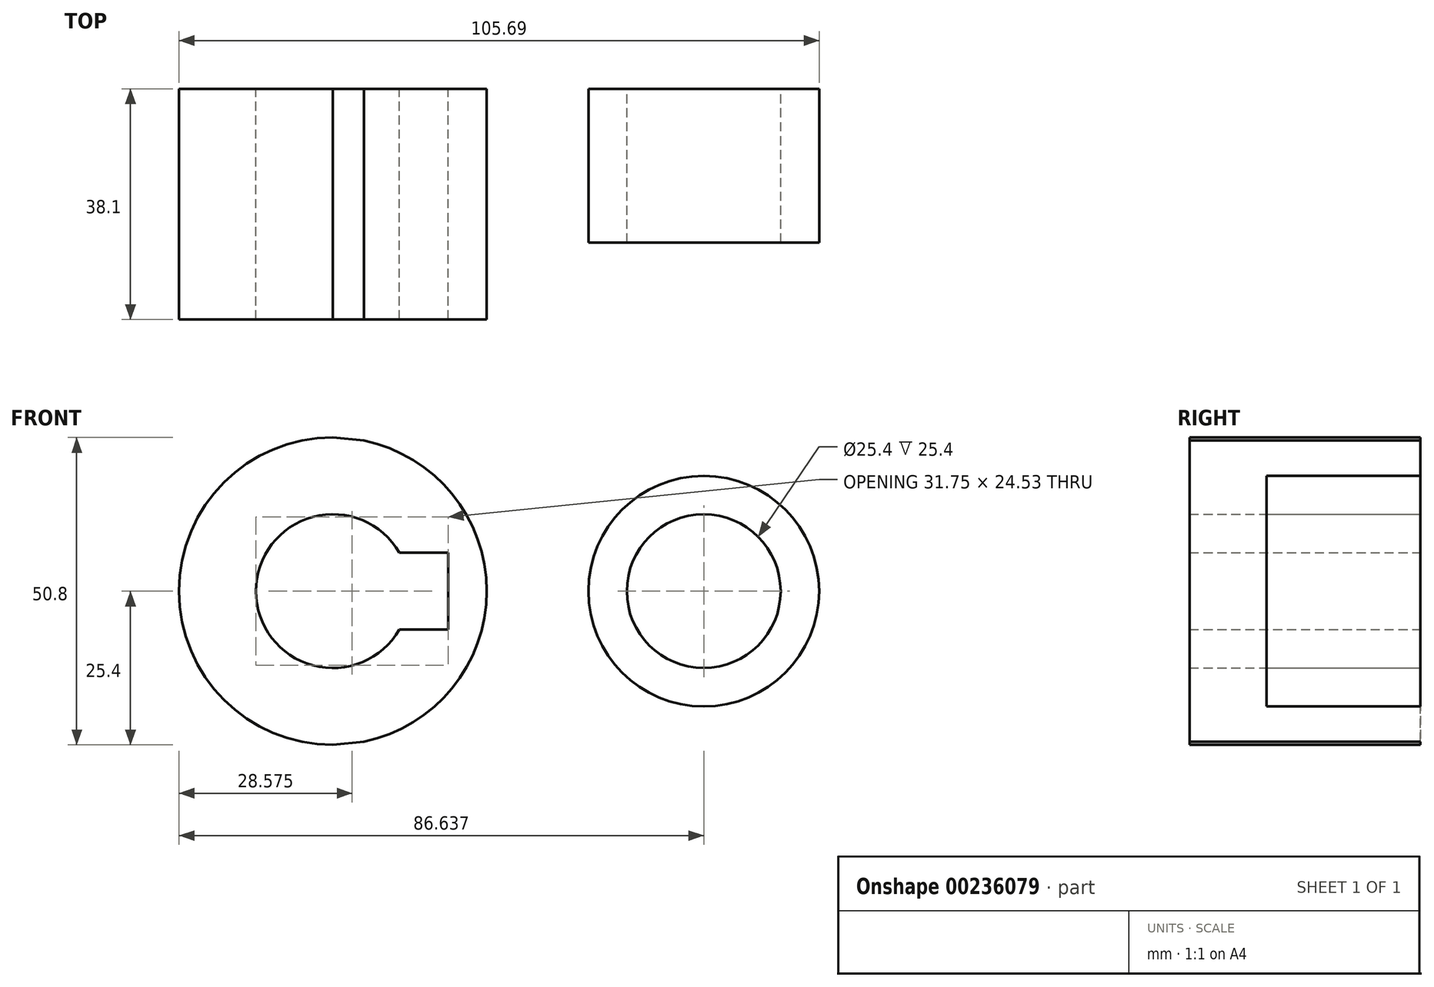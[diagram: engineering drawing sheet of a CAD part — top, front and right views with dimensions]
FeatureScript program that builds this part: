
annotation { "Feature Type Name" : "Feature", "Feature Type Description" : "" }
export const myFeature = defineFeature(function(context is Context, id is Id, definition is map)
    precondition{}
    {
        {
            var Q0;
            Q0=qCreatedBy(makeId("Front.planeOp"),FACE);
            var sketch = newSketch(context, id + "F0", { "sketchPlane" : qUnion([Q0])});
            skCircle(sketch, "E0", {"center": v(0, 0) * mm, "radius": 25.4 * mm});
            skCircle(sketch, "E1", {"center": v(61.24, 0) * mm, "radius": 19.05 * mm});
            skLineSegment(sketch, "E2", {"start": v(0, 25.4) * mm, "end": v(63.17, 18.95) * mm});
            skLineSegment(sketch, "E3", {"start": v(0, -25.4) * mm, "end": v(63.17, -18.95) * mm});
            skCircle(sketch, "E4", {"center": v(61.24, 0) * mm, "radius": 12.7 * mm});
            skCircle(sketch, "E5", {"center": v(0, 0) * mm, "radius": 12.7 * mm});
            skLineSegment(sketch, "E6.bottom", {"start": v(19.05, 6.35) * mm, "end": v(-19.05, 6.35) * mm});
            skLineSegment(sketch, "E6.top", {"start": v(19.05, -6.35) * mm, "end": v(-19.05, -6.35) * mm});
            skLineSegment(sketch, "E6.left", {"start": v(19.05, 6.35) * mm, "end": v(19.05, -6.35) * mm});
            skLineSegment(sketch, "E6.right", {"start": v(-19.05, 6.35) * mm, "end": v(-19.05, -6.35) * mm});
            skSolve(sketch);
        }
        {
            var Q0;
            {var subQ0=sQuery(id+"F0.wireOp",EDGE,"E2");var subQ1=sQuery(id+"F0.wireOp",EDGE,"E0");var subQ2=makeQuery(id+"F0.imprint","INTERSECT",VERTEX,{"disambiguationData":[OD(0.0)],"derivedFrom":[subQ1,subQ0]});Q0=makeQuery(id+"F0.imprint","IMPRINT",FACE,{"disambiguationData":[TD([[makeQuery(id+"F0.imprint","IMPRINT",EDGE,{"disambiguationData":[TD([[subQ2,1.0]])],"derivedFrom":subQ1}),1.0]])]});}
            var Q1;
            {var subQ0=sQuery(id+"F0.wireOp",EDGE,"E3");var subQ1=sQuery(id+"F0.wireOp",EDGE,"E0");var subQ2=makeQuery(id+"F0.imprint","INTERSECT",VERTEX,{"disambiguationData":[OD(0.0)],"derivedFrom":[subQ1,subQ0]});Q1=makeQuery(id+"F0.imprint","IMPRINT",FACE,{"disambiguationData":[TD([[makeQuery(id+"F0.imprint","IMPRINT",EDGE,{"disambiguationData":[TD([[subQ2,-1.0]])],"derivedFrom":subQ1}),1.0]])]});}
            var Q2;
            {var subQ0=sQuery(id+"F0.wireOp",EDGE,"E2");var subQ1=sQuery(id+"F0.wireOp",EDGE,"E0");var subQ2=makeQuery(id+"F0.imprint","INTERSECT",VERTEX,{"disambiguationData":[OD(1.0)],"derivedFrom":[subQ1,subQ0]});Q2=makeQuery(id+"F0.imprint","IMPRINT",FACE,{"disambiguationData":[TD([[makeQuery(id+"F0.imprint","IMPRINT",EDGE,{"disambiguationData":[TD([[subQ2,1.0]])],"derivedFrom":subQ1}),-1.0]])]});}
            var Q3;
            Q3=makeQuery(id+"F0.imprint","IMPRINT",FACE,{"disambiguationData":[TD([[makeQuery(id+"F0.imprint","IMPRINT",EDGE,{"derivedFrom":sQuery(id+"F0.wireOp",EDGE,"E4")}),-1.0]])]});
            var Q4;
            {var subQ5=sQuery(id+"F0.wireOp",EDGE,"E6.right");Q4=makeQuery(id+"F0.imprint","IMPRINT",FACE,{"disambiguationData":[TD([[makeQuery(id+"F0.imprint","IMPRINT",EDGE,{"derivedFrom":subQ5}),1.0]])]});}
            var Q5;
            {var subQ5=sQuery(id+"F0.wireOp",EDGE,"E6.left");Q5=makeQuery(id+"F0.imprint","IMPRINT",FACE,{"disambiguationData":[TD([[makeQuery(id+"F0.imprint","IMPRINT",EDGE,{"derivedFrom":subQ5}),1.0]])]});}
            extrude(context, id + "F1", {"entities" : qUnion([Q0, Q1, Q2, Q3, Q4, Q5]), "depth" : 25.4 * mm});
        }
        {
            var Q0;
            Q0=makeQuery(id+"F1.opExtrude","CAP_FACE",FACE,{"disambiguationData":[OSD([sQuery(id+"F0.wireOp",EDGE,"E0"),sQuery(id+"F0.wireOp",EDGE,"E1"),sQuery(id+"F0.wireOp",EDGE,"E2"),sQuery(id+"F0.wireOp",EDGE,"E3"),sQuery(id+"F0.wireOp",EDGE,"E4"),sQuery(id+"F0.wireOp",EDGE,"E5"),sQuery(id+"F0.wireOp",EDGE,"E6.bottom"),sQuery(id+"F0.wireOp",EDGE,"E6.top"),sQuery(id+"F0.wireOp",EDGE,"E6.left")])],"isStart":false});
            var sketch = newSketch(context, id + "F2", { "sketchPlane" : qUnion([Q0])});
            skCircle(sketch, "E7", {"center": v(0, 0) * mm, "radius": 25.4 * mm});
            skCircle(sketch, "E8", {"center": v(0, 0) * mm, "radius": 12.7 * mm});
            skLineSegment(sketch, "E9.bottom", {"start": v(19.05, 6.35) * mm, "end": v(-19.05, 6.35) * mm});
            skLineSegment(sketch, "E9.top", {"start": v(19.05, -6.35) * mm, "end": v(-19.05, -6.35) * mm});
            skLineSegment(sketch, "E9.left", {"start": v(19.05, 6.35) * mm, "end": v(19.05, -6.35) * mm});
            skLineSegment(sketch, "E9.right", {"start": v(-19.05, 6.35) * mm, "end": v(-19.05, -6.35) * mm});
            skSolve(sketch);
        }
        {
            var Q0;
            {var subQ5=sQuery(id+"F2.wireOp",EDGE,"E9.right");Q0=makeQuery(id+"F2.imprint","IMPRINT",FACE,{"disambiguationData":[TD([[makeQuery(id+"F2.imprint","IMPRINT",EDGE,{"derivedFrom":subQ5}),1.0]])]});}
            var Q1;
            {var subQ7=sQuery(id+"F2.wireOp",EDGE,"E9.left");Q1=makeQuery(id+"F2.imprint","IMPRINT",FACE,{"disambiguationData":[TD([[makeQuery(id+"F2.imprint","IMPRINT",EDGE,{"derivedFrom":subQ7}),1.0]])]});}
            extrude(context, id + "F3", {"entities" : qUnion([Q0, Q1]), "operationType" : NewBodyOperationType.ADD, "depth" : 12.7 * mm});
        }
    });
